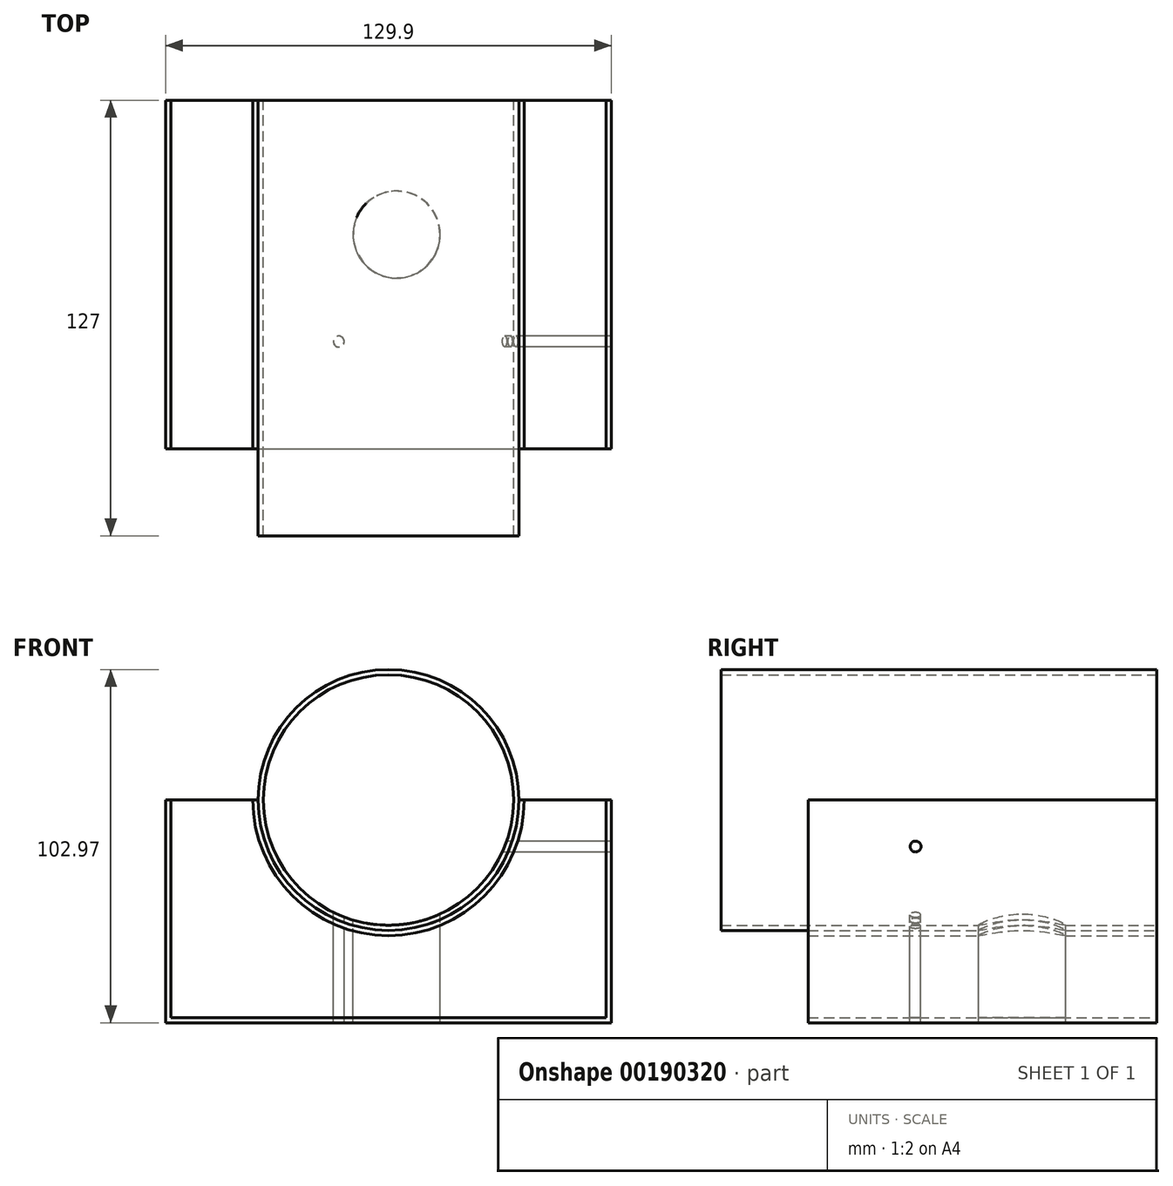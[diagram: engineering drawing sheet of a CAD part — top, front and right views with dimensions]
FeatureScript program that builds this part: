
annotation { "Feature Type Name" : "Feature", "Feature Type Description" : "" }
export const myFeature = defineFeature(function(context is Context, id is Id, definition is map)
    precondition{}
    {
        {
            var Q0;
            Q0=qCreatedBy(makeId("Front.planeOp"),FACE);
            var sketch = newSketch(context, id + "F0", { "sketchPlane" : qUnion([Q0])});
            skCircle(sketch, "E0", {"center": v(0, 0) * mm, "radius": 36.5 * mm});
            skCircle(sketch, "E1.0", {"center": v(0, 0) * mm, "radius": 38.02 * mm});
            skLineSegment(sketch, "E2", {"start": v(0, 0) * mm, "end": v(0, 36.5) * mm});
            skLineSegment(sketch, "E3", {"start": v(0, 0) * mm, "end": v(-31.6, -18.25) * mm});
            skLineSegment(sketch, "E4", {"start": v(0, 0) * mm, "end": v(31.6, -18.25) * mm});
            skSolve(sketch);
        }
        {
            var Q0;
            Q0=qCreatedBy(makeId("Right.planeOp"),FACE);
            var sketch = newSketch(context, id + "F1", { "sketchPlane" : qUnion([Q0])});
            skLineSegment(sketch, "E5", {"start": v(-51.87, -37.95) * mm, "end": v(-70.28, -37.95) * mm});
            skLineSegment(sketch, "E6", {"start": v(-70.28, -37.95) * mm, "end": v(-70.28, -13.57) * mm});
            skCircle(sketch, "E7", {"center": v(-70.28, -13.57) * mm, "radius": 1.59 * mm});
            skSolve(sketch);
        }
        {
            var Q0;
            Q0=makeQuery(id+"F0.imprint","IMPRINT",FACE,{"disambiguationData":[TD([[makeQuery(id+"F0.imprint","IMPRINT",EDGE,{"derivedFrom":sQuery(id+"F0.wireOp",EDGE,"E0")}),-1.0]])]});
            extrude(context, id + "F2", {"entities" : qUnion([Q0]), "depth" : 127 * mm});
        }
        {
            var Q0;
            Q0=qCreatedBy(makeId("Top.planeOp"),FACE);
            var sketch = newSketch(context, id + "F3", { "sketchPlane" : qUnion([Q0])});
            skCircle(sketch, "E8", {"center": v(2.36, -39.17) * mm, "radius": 12.7 * mm});
            skLineSegment(sketch, "E9", {"start": v(0, 0) * mm, "end": v(2.36, 0) * mm});
            skLineSegment(sketch, "E10", {"start": v(2.36, 0) * mm, "end": v(2.36, -57.65) * mm});
            skLineSegment(sketch, "E11", {"start": v(0, 0) * mm, "end": v(-14.48, 0) * mm});
            skLineSegment(sketch, "E12", {"start": v(-14.48, 0) * mm, "end": v(-14.48, -70.36) * mm});
            skCircle(sketch, "E13", {"center": v(-14.48, -70.36) * mm, "radius": 1.59 * mm});
            skSolve(sketch);
        }
        {
            var Q0;
            {var subQ0=sQuery(id+"F3.wireOp",EDGE,"E10");var subQ1=sQuery(id+"F3.wireOp",EDGE,"E8");var subQ2=makeQuery(id+"F3.imprint","INTERSECT",VERTEX,{"disambiguationData":[OD(0.0)],"derivedFrom":[subQ1,subQ0]});Q0=makeQuery(id+"F3.imprint","IMPRINT",FACE,{"disambiguationData":[TD([[makeQuery(id+"F3.imprint","IMPRINT",EDGE,{"disambiguationData":[TD([[subQ2,1.0]])],"derivedFrom":subQ1}),1.0]])]});}
            var Q1;
            {var subQ0=sQuery(id+"F3.wireOp",EDGE,"E10");var subQ1=sQuery(id+"F3.wireOp",EDGE,"E8");var subQ2=makeQuery(id+"F3.imprint","INTERSECT",VERTEX,{"disambiguationData":[OD(0.0)],"derivedFrom":[subQ1,subQ0]});Q1=makeQuery(id+"F3.imprint","IMPRINT",FACE,{"disambiguationData":[TD([[makeQuery(id+"F3.imprint","IMPRINT",EDGE,{"disambiguationData":[TD([[subQ2,-1.0]])],"derivedFrom":subQ1}),1.0]])]});}
            extrude(context, id + "F4", {"entities" : qUnion([Q0, Q1]), "oppositeDirection" : true, "depth" : 127 * mm});
        }
        {
            var Q0;
            Q0=makeQuery(id+"F3.imprint","IMPRINT",FACE,{"disambiguationData":[TD([[makeQuery(id+"F3.imprint","IMPRINT",EDGE,{"derivedFrom":sQuery(id+"F3.wireOp",EDGE,"E13")}),1.0]])]});
            extrude(context, id + "F5", {"entities" : qUnion([Q0]), "oppositeDirection" : true, "depth" : 127 * mm});
        }
        {
            var Q0;
            Q0=makeQuery(id+"F1.imprint","IMPRINT",FACE,{"disambiguationData":[TD([[makeQuery(id+"F1.imprint","IMPRINT",EDGE,{"derivedFrom":sQuery(id+"F1.wireOp",EDGE,"E7")}),1.0]])]});
            extrude(context, id + "F6", {"entities" : qUnion([Q0]), "depth" : 127 * mm});
        }
        {
            var Q0;
            Q0=makeQuery(id+"F4.opExtrude","SWEPT_BODY",BODY,{"disambiguationData":[OSD([sQuery(id+"F3.wireOp",EDGE,"E8")])]});
            var Q1;
            Q1=makeQuery(id+"F5.opExtrude","SWEPT_BODY",BODY,{"disambiguationData":[OSD([sQuery(id+"F3.wireOp",EDGE,"E13")])]});
            var Q2;
            Q2=makeQuery(id+"F6.opExtrude","SWEPT_BODY",BODY,{"disambiguationData":[OSD([sQuery(id+"F1.wireOp",EDGE,"E7")])]});
            var Q3;
            Q3=makeQuery(id+"F2.opExtrude","SWEPT_BODY",BODY,{"disambiguationData":[OSD([sQuery(id+"F0.wireOp",EDGE,"E0"),sQuery(id+"F0.wireOp",EDGE,"E1.0")])]});
            booleanBodies(context, id + "F7", {"operationType" : BooleanOperationType.SUBTRACTION, "tools" : qUnion([Q0, Q1, Q2]), "targets" : qUnion([Q3]), "keepTools" : true});
        }
        {
            var Q0;
            Q0=qCreatedBy(makeId("Front.planeOp"),FACE);
            var sketch = newSketch(context, id + "F8", { "sketchPlane" : qUnion([Q0])});
            skCircle(sketch, "E14.0", {"center": v(0, 0) * mm, "radius": 38.02 * mm});
            skLineSegment(sketch, "E15", {"start": v(0, -38.02) * mm, "end": v(0, -63.42) * mm});
            skLineSegment(sketch, "E16", {"start": v(-38.02, 0) * mm, "end": v(-63.42, 0) * mm});
            skLineSegment(sketch, "E17", {"start": v(38.02, 0) * mm, "end": v(63.42, 0) * mm});
            skLineSegment(sketch, "E18", {"start": v(-63.42, 0) * mm, "end": v(-63.42, -63.42) * mm});
            skLineSegment(sketch, "E19", {"start": v(-63.42, -63.42) * mm, "end": v(63.42, -63.42) * mm});
            skLineSegment(sketch, "E20", {"start": v(63.42, -63.42) * mm, "end": v(63.42, 0) * mm});
            skSolve(sketch);
        }
        {
            var Q0;
            {var subQ2=sQuery(id+"F8.wireOp",EDGE,"E15");Q0=makeQuery(id+"F8.imprint","IMPRINT",FACE,{"disambiguationData":[TD([[makeQuery(id+"F8.imprint","IMPRINT",EDGE,{"derivedFrom":subQ2}),-1.0]])]});}
            var Q1;
            {var subQ1=sQuery(id+"F8.wireOp",EDGE,"E15");Q1=makeQuery(id+"F8.imprint","IMPRINT",FACE,{"disambiguationData":[TD([[makeQuery(id+"F8.imprint","IMPRINT",EDGE,{"derivedFrom":subQ1}),1.0]])]});}
            extrude(context, id + "F9", {"entities" : qUnion([Q0, Q1]), "depth" : 101.6 * mm});
        }
        {
            var Q0;
            Q0=makeQuery(id+"F5.opExtrude","SWEPT_BODY",BODY,{"disambiguationData":[OSD([sQuery(id+"F3.wireOp",EDGE,"E13")])]});
            var Q1;
            Q1=makeQuery(id+"F4.opExtrude","SWEPT_BODY",BODY,{"disambiguationData":[OSD([sQuery(id+"F3.wireOp",EDGE,"E8")])]});
            var Q2;
            Q2=makeQuery(id+"F6.opExtrude","SWEPT_BODY",BODY,{"disambiguationData":[OSD([sQuery(id+"F1.wireOp",EDGE,"E7")])]});
            var Q3;
            Q3=makeQuery(id+"F9.opExtrude","SWEPT_BODY",BODY,{"disambiguationData":[OSD([sQuery(id+"F8.wireOp",EDGE,"E14.0"),sQuery(id+"F8.wireOp",EDGE,"E16"),sQuery(id+"F8.wireOp",EDGE,"E17"),sQuery(id+"F8.wireOp",EDGE,"E18"),sQuery(id+"F8.wireOp",EDGE,"E19"),sQuery(id+"F8.wireOp",EDGE,"E20")])]});
            booleanBodies(context, id + "F10", {"operationType" : BooleanOperationType.SUBTRACTION, "tools" : qUnion([Q0, Q1, Q2]), "targets" : qUnion([Q3]), "keepTools" : true});
        }
        {
            var Q0;
            Q0=qCreatedBy(makeId("Front.planeOp"),FACE);
            var sketch = newSketch(context, id + "F11", { "sketchPlane" : qUnion([Q0])});
            skCircle(sketch, "E21.0", {"center": v(0, 0) * mm, "radius": 38.02 * mm});
            skLineSegment(sketch, "E22", {"start": v(-38.02, 0) * mm, "end": v(-39.55, 0) * mm});
            skCircle(sketch, "E23", {"center": v(0, 0) * mm, "radius": 39.55 * mm});
            skLineSegment(sketch, "E24", {"start": v(-39.55, 0) * mm, "end": v(-64.95, 0) * mm});
            skLineSegment(sketch, "E25", {"start": v(-64.95, 0) * mm, "end": v(-64.95, -64.95) * mm});
            skLineSegment(sketch, "E26", {"start": v(-64.95, -64.95) * mm, "end": v(64.95, -64.95) * mm});
            skLineSegment(sketch, "E27", {"start": v(64.95, -64.95) * mm, "end": v(64.95, 0) * mm});
            skLineSegment(sketch, "E28", {"start": v(64.95, 0) * mm, "end": v(39.55, 0) * mm});
            skSolve(sketch);
        }
        {
            var Q0;
            {var subQ0=sQuery(id+"F11.wireOp",EDGE,"E24");Q0=makeQuery(id+"F11.imprint","IMPRINT",FACE,{"disambiguationData":[TD([[makeQuery(id+"F11.imprint","IMPRINT",EDGE,{"derivedFrom":subQ0}),1.0]])]});}
            extrude(context, id + "F12", {"entities" : qUnion([Q0]), "depth" : 101.6 * mm});
        }
        {
            var Q0;
            Q0=makeQuery(id+"F5.opExtrude","SWEPT_BODY",BODY,{"disambiguationData":[OSD([sQuery(id+"F3.wireOp",EDGE,"E13")])]});
            var Q1;
            Q1=makeQuery(id+"F4.opExtrude","SWEPT_BODY",BODY,{"disambiguationData":[OSD([sQuery(id+"F3.wireOp",EDGE,"E8")])]});
            var Q2;
            Q2=makeQuery(id+"F6.opExtrude","SWEPT_BODY",BODY,{"disambiguationData":[OSD([sQuery(id+"F1.wireOp",EDGE,"E7")])]});
            var Q3;
            Q3=makeQuery(id+"F12.opExtrude","SWEPT_BODY",BODY,{"disambiguationData":[OSD([sQuery(id+"F11.wireOp",EDGE,"E23"),sQuery(id+"F11.wireOp",EDGE,"E24"),sQuery(id+"F11.wireOp",EDGE,"E25"),sQuery(id+"F11.wireOp",EDGE,"E26"),sQuery(id+"F11.wireOp",EDGE,"E27"),sQuery(id+"F11.wireOp",EDGE,"E28")])]});
            booleanBodies(context, id + "F13", {"operationType" : BooleanOperationType.SUBTRACTION, "tools" : qUnion([Q0, Q1, Q2]), "targets" : qUnion([Q3])});
        }
    });
